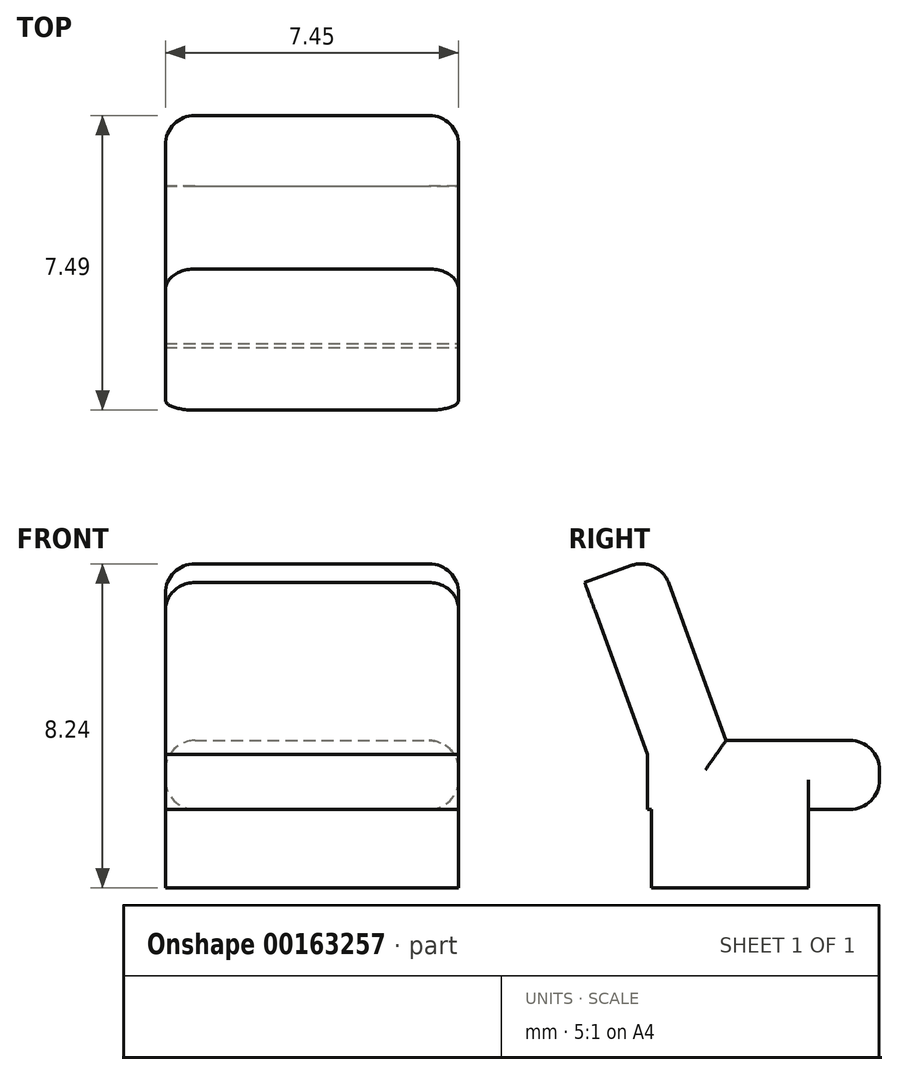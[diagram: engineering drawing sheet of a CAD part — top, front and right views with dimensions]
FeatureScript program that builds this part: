
annotation { "Feature Type Name" : "Feature", "Feature Type Description" : "" }
export const myFeature = defineFeature(function(context is Context, id is Id, definition is map)
    precondition{}
    {
        {
            var Q0;
            Q0=qCreatedBy(makeId("Top.planeOp"),FACE);
            var sketch = newSketch(context, id + "F0", { "sketchPlane" : qUnion([Q0])});
            skLineSegment(sketch, "E0.bottom", {"start": v(0, 0) * mm, "end": v(7.45, 0) * mm});
            skLineSegment(sketch, "E0.top", {"start": v(0, 4) * mm, "end": v(7.45, 4) * mm});
            skLineSegment(sketch, "E0.left", {"start": v(0, 0) * mm, "end": v(0, 4) * mm});
            skLineSegment(sketch, "E0.right", {"start": v(7.45, 0) * mm, "end": v(7.45, 4) * mm});
            skSolve(sketch);
        }
        {
            var Q0;
            Q0 = qSketchRegion(id + "F0", true);
            extrude(context, id + "F1", {"entities" : qUnion([Q0]), "depth" : 2 * mm});
        }
        {
            var Q0;
            Q0=makeQuery(id+"F1.opExtrude","CAP_FACE",FACE,{"disambiguationData":[OSD([sQuery(id+"F0.wireOp",EDGE,"E0.bottom"),sQuery(id+"F0.wireOp",EDGE,"E0.top"),sQuery(id+"F0.wireOp",EDGE,"E0.left"),sQuery(id+"F0.wireOp",EDGE,"E0.right")])],"isStart":false});
            var sketch = newSketch(context, id + "F2", { "sketchPlane" : qUnion([Q0])});
            skLineSegment(sketch, "E1.bottom", {"start": v(0, 5.8) * mm, "end": v(7.45, 5.8) * mm});
            skLineSegment(sketch, "E1.top", {"start": v(0, -0.1) * mm, "end": v(7.45, -0.1) * mm});
            skLineSegment(sketch, "E1.left", {"start": v(0, 5.8) * mm, "end": v(0, -0.1) * mm});
            skLineSegment(sketch, "E1.right", {"start": v(7.45, 5.8) * mm, "end": v(7.45, -0.1) * mm});
            skSolve(sketch);
        }
        {
            var Q0;
            Q0 = qSketchRegion(id + "F2", true);
            extrude(context, id + "F3", {"entities" : qUnion([Q0]), "operationType" : NewBodyOperationType.ADD, "depth" : 1.75 * mm});
        }
        {
            var Q0;
            Q0=makeQuery(id+"F3.opExtrude","CAP_FACE",FACE,{"disambiguationData":[OSD([sQuery(id+"F2.wireOp",EDGE,"E1.bottom"),sQuery(id+"F2.wireOp",EDGE,"E1.top"),sQuery(id+"F2.wireOp",EDGE,"E1.left"),sQuery(id+"F2.wireOp",EDGE,"E1.right")])],"isStart":false});
            var sketch = newSketch(context, id + "F4", { "sketchPlane" : qUnion([Q0])});
            skLineSegment(sketch, "E2", {"start": v(0, 1.9) * mm, "end": v(7.45, 1.9) * mm, "construction": true});
            skSolve(sketch);
        }
        {
            var Q0;
            Q0=sQuery(id+"F4.wireOp",EDGE,"E2");
            cPlane(context, id + "F5", {"entities" : qUnion([Q0]), "cplaneType" : CPlaneType.LINE_ANGLE, "offset" : 25 * mm, "angle" : 20 * degree, "width" : 150 * mm, "height" : 150 * mm});
        }
        {
            var Q0;
            Q0=qCreatedBy(id+"F5.planeOp",FACE);
            var sketch = newSketch(context, id + "F6", { "sketchPlane" : qUnion([Q0])});
            skLineSegment(sketch, "E3.bottom", {"start": v(0, 2.87) * mm, "end": v(-7.45, 2.87) * mm});
            skLineSegment(sketch, "E3.top", {"start": v(0, 7.87) * mm, "end": v(-7.45, 7.87) * mm});
            skLineSegment(sketch, "E3.left", {"start": v(0, 2.87) * mm, "end": v(0, 7.87) * mm});
            skLineSegment(sketch, "E3.right", {"start": v(-7.45, 2.87) * mm, "end": v(-7.45, 7.87) * mm});
            skSolve(sketch);
        }
        {
            var Q0;
            Q0 = qSketchRegion(id + "F6", true);
            extrude(context, id + "F7", {"entities" : qUnion([Q0]), "operationType" : NewBodyOperationType.ADD, "oppositeDirection" : true, "depth" : 2 * mm});
        }
        {
            var Q0;
            Q0=makeQuery(id+"F3.opExtrude","SWEPT_EDGE",EDGE,{"disambiguationData":[OSD([sQuery(id+"F2.wireOp",EDGE,"E1.bottom"),sQuery(id+"F2.wireOp",EDGE,"E1.right")])]});
            var Q1;
            Q1=makeQuery(id+"F3.opExtrude","CAP_EDGE",EDGE,{"disambiguationData":[OSD([sQuery(id+"F2.wireOp",EDGE,"E1.right")])],"isStart":false});
            var Q2;
            Q2=makeQuery(id+"F3.opExtrude","CAP_EDGE",EDGE,{"disambiguationData":[OSD([sQuery(id+"F2.wireOp",EDGE,"E1.bottom")])],"isStart":false});
            var Q3;
            Q3=makeQuery(id+"F3.opExtrude","CAP_EDGE",EDGE,{"disambiguationData":[OSD([sQuery(id+"F2.wireOp",EDGE,"E1.bottom")])],"isStart":true});
            var Q4;
            Q4=makeQuery(id+"F3.opExtrude","SWEPT_EDGE",EDGE,{"disambiguationData":[OSD([sQuery(id+"F2.wireOp",EDGE,"E1.bottom"),sQuery(id+"F2.wireOp",EDGE,"E1.left")])]});
            var Q5;
            Q5=makeQuery(id+"F3.opExtrude","CAP_EDGE",EDGE,{"disambiguationData":[OSD([sQuery(id+"F2.wireOp",EDGE,"E1.left")])],"isStart":false});
            var Q6;
            {var subQ0=sQuery(id+"F2.wireOp",EDGE,"E1.left");Q6=makeQuery(id+"F3.boolean.opBoolean","SPLIT",EDGE,{"disambiguationData":[TD([makeQuery(id+"F1.opExtrude","SWEPT_FACE",FACE,{"disambiguationData":[OSD([sQuery(id+"F0.wireOp",EDGE,"E0.top")])]})])],"derivedFrom":makeQuery(id+"F3.opExtrude","CAP_EDGE",EDGE,{"disambiguationData":[OSD([subQ0])],"isStart":true})});}
            var Q7;
            Q7=makeQuery(id+"F7.opExtrude","CAP_EDGE",EDGE,{"disambiguationData":[OSD([sQuery(id+"F6.wireOp",EDGE,"E3.left")])],"isStart":true});
            var Q8;
            Q8=makeQuery(id+"F7.opExtrude","CAP_EDGE",EDGE,{"disambiguationData":[OSD([sQuery(id+"F6.wireOp",EDGE,"E3.top")])],"isStart":true});
            var Q9;
            Q9=makeQuery(id+"F7.opExtrude","CAP_EDGE",EDGE,{"disambiguationData":[OSD([sQuery(id+"F6.wireOp",EDGE,"E3.right")])],"isStart":true});
            var Q10;
            Q10=makeQuery(id+"F7.opExtrude","SWEPT_EDGE",EDGE,{"disambiguationData":[OSD([sQuery(id+"F6.wireOp",EDGE,"E3.top"),sQuery(id+"F6.wireOp",EDGE,"E3.right")])]});
            var Q11;
            Q11=makeQuery(id+"F7.opExtrude","SWEPT_EDGE",EDGE,{"disambiguationData":[OSD([sQuery(id+"F6.wireOp",EDGE,"E3.top"),sQuery(id+"F6.wireOp",EDGE,"E3.left")])]});
            fillet(context, id + "F8", {"entities" : qUnion([Q0, Q1, Q2, Q3, Q4, Q5, Q6, Q7, Q8, Q9, Q10, Q11]), "radius" : .75 * mm, "tangentPropagation" : true, "allowEdgeOverflow" : false});
        }
        {
            var Q0;
            {var subQ0=sQuery(id+"F2.wireOp",EDGE,"E1.bottom");Q0=makeQuery(id+"F8.opFillet","BLEND_EDGE",EDGE,{"blendedFrom":[makeQuery(id+"F3.opExtrude","SWEPT_EDGE",EDGE,{"disambiguationData":[OSD([subQ0,sQuery(id+"F2.wireOp",EDGE,"E1.right")])]}),makeQuery(id+"F3.opExtrude","CAP_EDGE",EDGE,{"disambiguationData":[OSD([subQ0])],"isStart":true})],"blendedInto":[]});}
            fillet(context, id + "F9", {"entities" : qUnion([Q0]), "radius" : .75 * mm, "tangentPropagation" : true, "allowEdgeOverflow" : false});
        }
    });
